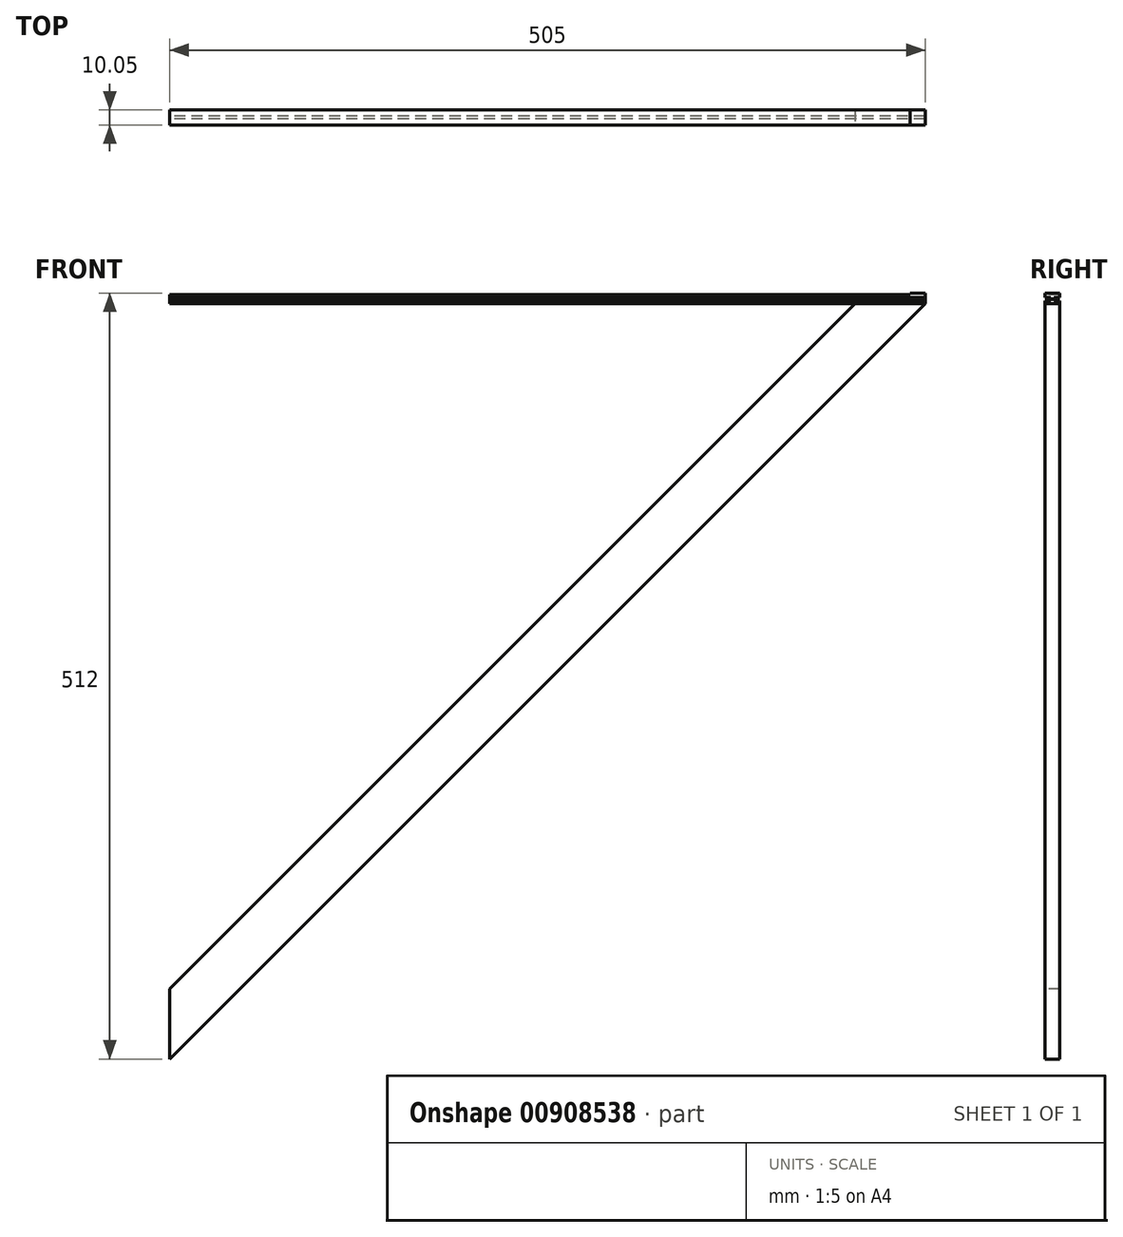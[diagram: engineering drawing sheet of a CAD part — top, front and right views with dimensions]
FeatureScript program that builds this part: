
annotation { "Feature Type Name" : "Feature", "Feature Type Description" : "" }
export const myFeature = defineFeature(function(context is Context, id is Id, definition is map)
    precondition{}
    {
        {
            var Q0;
            Q0=qCreatedBy(makeId("Right.planeOp"),FACE);
            var sketch = newSketch(context, id + "F0", { "sketchPlane" : qUnion([Q0])});
            skLineSegment(sketch, "E0", {"start": v(0, 0) * mm, "end": v(-1, 0) * mm});
            skLineSegment(sketch, "E1", {"start": v(-1, 0) * mm, "end": v(-1, 1) * mm});
            skLineSegment(sketch, "E2", {"start": v(-1, 1) * mm, "end": v(-5, 1) * mm});
            skLineSegment(sketch, "E3", {"start": v(-5, 1) * mm, "end": v(-5, 3) * mm});
            skLineSegment(sketch, "E4", {"start": v(-5, 3) * mm, "end": v(0, 3) * mm});
            skLineSegment(sketch, "E5.MirrorCS", {"start": v(5, 3) * mm, "end": v(0, 3) * mm});
            skLineSegment(sketch, "E6.MirrorCS", {"start": v(5, 1) * mm, "end": v(5, 3) * mm});
            skLineSegment(sketch, "E7.MirrorCS", {"start": v(1, 1) * mm, "end": v(5, 1) * mm});
            skLineSegment(sketch, "E8.MirrorCS", {"start": v(1, 0) * mm, "end": v(1, 1) * mm});
            skLineSegment(sketch, "E9.MirrorCS", {"start": v(1, 0) * mm, "end": v(1, -1) * mm});
            skLineSegment(sketch, "E10.MirrorCS", {"start": v(1, -1) * mm, "end": v(5, -1) * mm});
            skLineSegment(sketch, "E11.MirrorCS", {"start": v(5, -1) * mm, "end": v(5, -3) * mm});
            skLineSegment(sketch, "E12.MirrorCS", {"start": v(5, -3) * mm, "end": v(0, -3) * mm});
            skLineSegment(sketch, "E13.MirrorCS", {"start": v(-5, -3) * mm, "end": v(0, -3) * mm});
            skLineSegment(sketch, "E14.MirrorCS", {"start": v(-5, -1) * mm, "end": v(-5, -3) * mm});
            skLineSegment(sketch, "E15.MirrorCS", {"start": v(-1, -1) * mm, "end": v(-5, -1) * mm});
            skLineSegment(sketch, "E16.MirrorCS", {"start": v(-1, 0) * mm, "end": v(-1, -1) * mm});
            skSolve(sketch);
        }
        {
            var Q0;
            Q0 = qSketchRegion(id + "F0", true);
            extrude(context, id + "F1", {"entities" : qUnion([Q0]), "depth" : 505 * mm, "offsetDistance" : 25 * mm});
        }
        {
            var Q0;
            Q0=makeQuery(id+"F1.opExtrude","SWEPT_FACE",FACE,{"disambiguationData":[OSD([sQuery(id+"F0.wireOp",EDGE,"E4"),sQuery(id+"F0.wireOp",EDGE,"E5.MirrorCS")])]});
            var sketch = newSketch(context, id + "F2", { "sketchPlane" : qUnion([Q0])});
            skLineSegment(sketch, "E17", {"start": v(505, 5) * mm, "end": v(495, 5) * mm});
            skLineSegment(sketch, "E18", {"start": v(495, 5) * mm, "end": v(495, -5) * mm});
            skLineSegment(sketch, "E19", {"start": v(505, 5) * mm, "end": v(505, -5) * mm});
            skLineSegment(sketch, "E20", {"start": v(505, -5) * mm, "end": v(495, -5) * mm});
            skSolve(sketch);
        }
        {
            var Q0;
            Q0 = qSketchRegion(id + "F2", true);
            extrude(context, id + "F3", {"entities" : qUnion([Q0]), "operationType" : NewBodyOperationType.ADD, "depth" : 1 * mm, "offsetDistance" : 25 * mm});
        }
        {
            var Q0;
            Q0=qCreatedBy(makeId("Right.planeOp"),FACE);
            var sketch = newSketch(context, id + "F4", { "sketchPlane" : qUnion([Q0])});
            skLineSegment(sketch, "E21", {"start": v(-4.95, -3) * mm, "end": v(5.05, -3) * mm});
            skLineSegment(sketch, "E22", {"start": v(-4.95, -3) * mm, "end": v(-4.95, -508) * mm});
            skLineSegment(sketch, "E23", {"start": v(-4.95, -508) * mm, "end": v(5.05, -508) * mm});
            skLineSegment(sketch, "E24", {"start": v(5.05, -508) * mm, "end": v(5.05, -3) * mm});
            skSolve(sketch);
        }
        {
            var Q0;
            Q0 = qSketchRegion(id + "F4", true);
            extrude(context, id + "F5", {"entities" : qUnion([Q0]), "depth" : 505 * mm, "offsetDistance" : 25 * mm});
        }
        {
            var Q0;
            Q0=makeQuery(id+"F5.opExtrude","SWEPT_FACE",FACE,{"disambiguationData":[OSD([sQuery(id+"F4.wireOp",EDGE,"E22")])]});
            var sketch = newSketch(context, id + "F6", { "sketchPlane" : qUnion([Q0])});
            skLineSegment(sketch, "E25", {"start": v(0, -3) * mm, "end": v(0, -461) * mm});
            skLineSegment(sketch, "E26", {"start": v(0, -3) * mm, "end": v(458, -3) * mm});
            skLineSegment(sketch, "E27", {"start": v(458, -3) * mm, "end": v(0, -461) * mm});
            skSolve(sketch);
        }
        {
            var Q0;
            Q0 = qSketchRegion(id + "F6", true);
            extrude(context, id + "F7", {"entities" : qUnion([Q0]), "operationType" : NewBodyOperationType.REMOVE, "endBound" : BoundingType.THROUGH_ALL, "oppositeDirection" : true, "depth" : 25 * mm, "offsetDistance" : 25 * mm});
        }
        {
            var Q0;
            Q0=makeQuery(id+"F5.opExtrude","SWEPT_FACE",FACE,{"disambiguationData":[OSD([sQuery(id+"F4.wireOp",EDGE,"E22")])]});
            var sketch = newSketch(context, id + "F8", { "sketchPlane" : qUnion([Q0])});
            skLineSegment(sketch, "E28", {"start": v(0, -508) * mm, "end": v(505, -3) * mm});
            skLineSegment(sketch, "E29", {"start": v(505, -3) * mm, "end": v(505, -508) * mm});
            skLineSegment(sketch, "E30", {"start": v(505, -508) * mm, "end": v(0, -508) * mm});
            skSolve(sketch);
        }
        {
            var Q0;
            Q0 = qSketchRegion(id + "F8", true);
            extrude(context, id + "F9", {"entities" : qUnion([Q0]), "operationType" : NewBodyOperationType.REMOVE, "endBound" : BoundingType.THROUGH_ALL, "oppositeDirection" : true, "depth" : 25 * mm, "offsetDistance" : 25 * mm});
        }
    });
